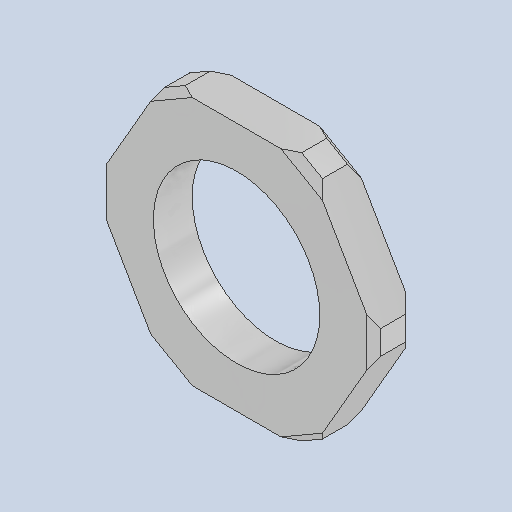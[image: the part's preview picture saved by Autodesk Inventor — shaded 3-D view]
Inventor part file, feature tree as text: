
AUTODESK INVENTOR PART (.ipt)
format: ipt  version: 2024.2 (Build 282272000, 272)  size: 137,216 bytes
history: native  units: mm
features: extrude x2, chamfer x2, sketch x1
ambient origin geometry x8: Origin, YZ Plane, XZ Plane, XY Plane, X Axis, Y Axis, Z Axis, Center Point
bodies: Solid1 (feature_tree)
feature tree (5):
  extrude  "Extrusion1"  Depth=2.8mm TaperAngle=0.0deg
  extrude  "Extrusion2"  Depth=2.8mm
  chamfer  "Chamfer1"  Distance=2.8mm
  chamfer  "Chamfer2"  Distance=1.0mm Angle=45.0deg
  sketch  "Sketch1"  dims[d0=18.0mm d1=2.8mm d2=0.0mm d3=12.0mm d4=2.8mm d5=0.0mm d6=1.0mm d7=2.0mm d8=45.0deg d9=0.5mm d10=2.0mm d11=45.0deg]
